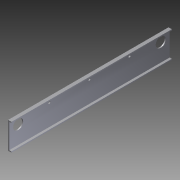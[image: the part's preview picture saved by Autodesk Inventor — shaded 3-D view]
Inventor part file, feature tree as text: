
AUTODESK INVENTOR PART (.ipt)
format: ipt  version: 2012 (Build 160160000, 160)  size: 107,008 bytes
history: native  units: in
note: dims shown in document units (in); Inventor stores cm internally (conversion verified against a paired STEP export)
features: extrude x2, sketch x2
ambient origin geometry x8: Origin, YZ Plane, XZ Plane, XY Plane, X Axis, Y Axis, Z Axis, Center Point
bodies: Solid1 (feature_tree)
feature tree (4):
  extrude  "Extrusion1"  Depth=0.125in
  extrude  "Extrusion2"  Depth=3.0in
  sketch  "Sketch1"  dims[d0=0.125in d2=0.125in]
  sketch  "Sketch2"  dims[d3=0.125in d4=3.0in d5=0.375in d6=18.0in d7=0.0in d8=1.125in d10=2.125in d11=1.0in d12=20.0in d13=0.0in d14=1.0in d15=2.125in d16=1.125in d17=0.25in d18=0.5in d19=9.0in d20=4.5in d21=4.5in d22=0.25in d23=0.25in d24=18.0in]
